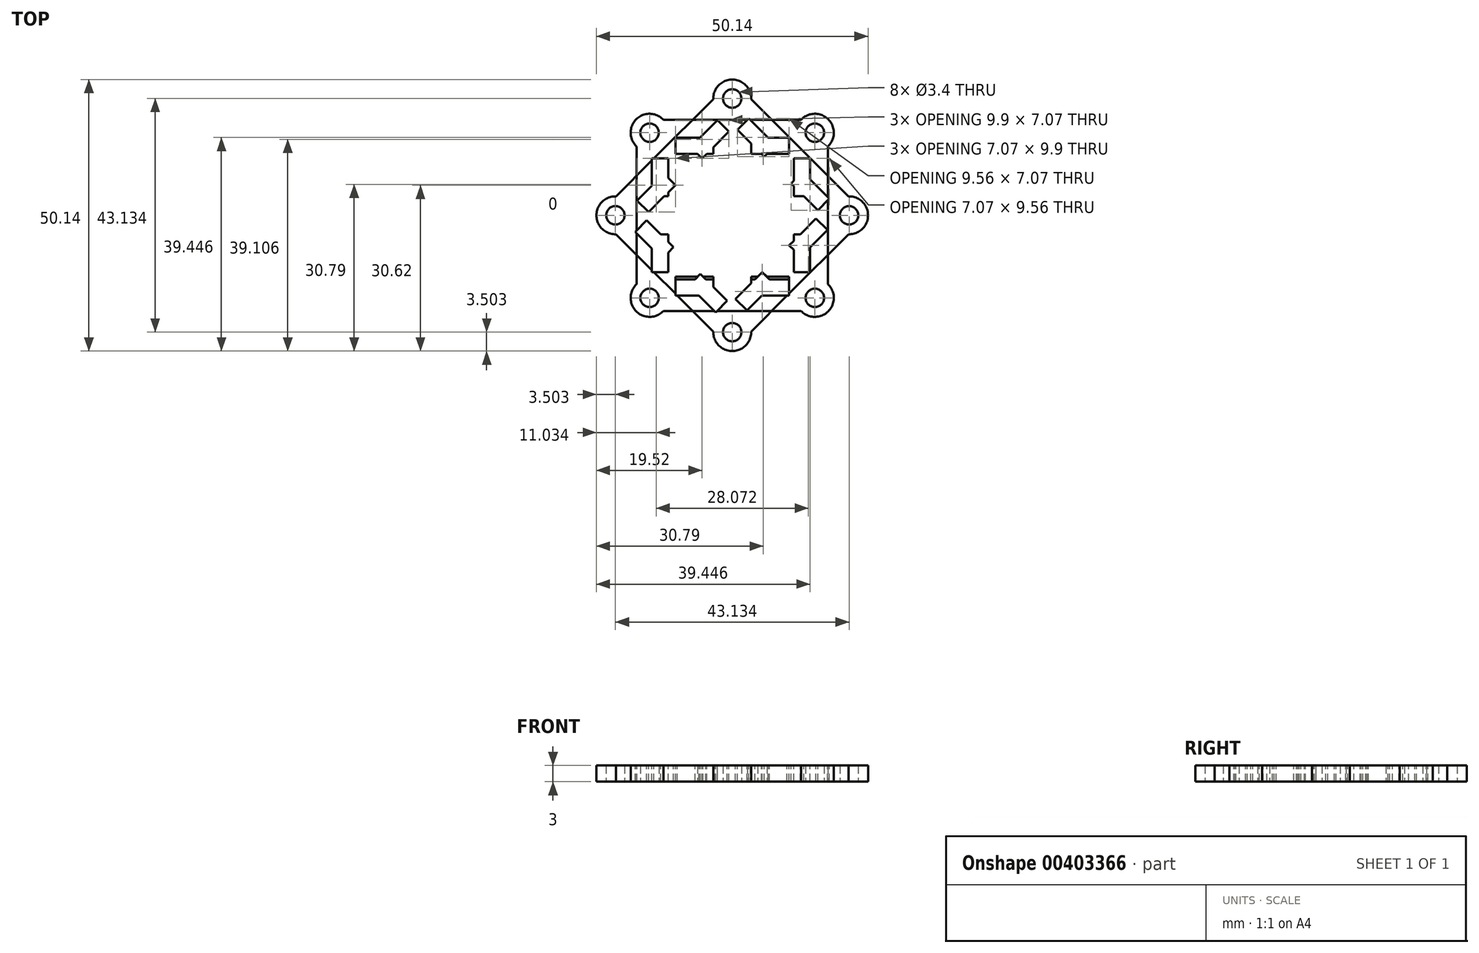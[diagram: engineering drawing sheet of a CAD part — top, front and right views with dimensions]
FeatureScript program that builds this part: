
annotation { "Feature Type Name" : "Feature", "Feature Type Description" : "" }
export const myFeature = defineFeature(function(context is Context, id is Id, definition is map)
    precondition{}
    {
        {
            assignVariable(context, id + "F0", {"name" : "padThickness", "anyValue" : 3});
        }
        {
            var Q0;
            Q0=qCreatedBy(makeId("Top.planeOp"),FACE);
            var sketch = newSketch(context, id + "F1", { "sketchPlane" : qUnion([Q0])});
            skLineSegment(sketch, "E0.bottom", {"start": v(15.25, -15.25) * mm, "end": v(-15.25, -15.25) * mm});
            skLineSegment(sketch, "E0.top", {"start": v(15.25, 15.25) * mm, "end": v(-15.25, 15.25) * mm});
            skLineSegment(sketch, "E0.left", {"start": v(15.25, -15.25) * mm, "end": v(15.25, 15.25) * mm});
            skLineSegment(sketch, "E0.right", {"start": v(-15.25, -15.25) * mm, "end": v(-15.25, 15.25) * mm});
            skPoint(sketch, "E0.middle", {"position": v(0, 0) * mm});
            skCircle(sketch, "E1", {"center": v(-15.25, 15.25) * mm, "radius": 1.7 * mm});
            skLineSegment(sketch, "E2", {"start": v(0, 15.25) * mm, "end": v(0, -15.25) * mm, "construction": true});
            skLineSegment(sketch, "E3", {"start": v(-15.25, 0) * mm, "end": v(15.25, 0) * mm, "construction": true});
            skCircle(sketch, "E4.MirrorC", {"center": v(15.25, 15.25) * mm, "radius": 1.7 * mm});
            skLineSegment(sketch, "E5.MirrorCS", {"start": v(15.25, 0) * mm, "end": v(-15.25, 0) * mm, "construction": true});
            skCircle(sketch, "E6.MirrorC", {"center": v(15.25, -15.25) * mm, "radius": 1.7 * mm});
            skCircle(sketch, "E7.MirrorC", {"center": v(-15.25, -15.25) * mm, "radius": 1.7 * mm});
            skCircle(sketch, "E8", {"center": v(-15.25, 15.25) * mm, "radius": 3.5 * mm});
            skCircle(sketch, "E9.MirrorC", {"center": v(15.25, 15.25) * mm, "radius": 3.5 * mm});
            skCircle(sketch, "E10.MirrorC", {"center": v(15.25, -15.25) * mm, "radius": 3.5 * mm});
            skCircle(sketch, "E11.MirrorC", {"center": v(-15.25, -15.25) * mm, "radius": 3.5 * mm});
            skLineSegment(sketch, "E12", {"start": v(-10.5, 15.25) * mm, "end": v(-10.5, -15.25) * mm, "construction": true});
            skLineSegment(sketch, "E13", {"start": v(10.5, 15.25) * mm, "end": v(10.5, -15.25) * mm, "construction": true});
            skLineSegment(sketch, "E14", {"start": v(-15.25, 17) * mm, "end": v(15.25, 17) * mm, "construction": true});
            skLineSegment(sketch, "E15", {"start": v(-15.25, -17) * mm, "end": v(15.25, -17) * mm, "construction": true});
            skLineSegment(sketch, "E16", {"start": v(-17.65, 12.7) * mm, "end": v(-17.65, -12.7) * mm});
            skLineSegment(sketch, "E17", {"start": v(-12.85, -12.7) * mm, "end": v(-12.85, 12.7) * mm});
            skLineSegment(sketch, "E18", {"start": v(-12.7, 17.65) * mm, "end": v(12.7, 17.65) * mm});
            skLineSegment(sketch, "E19", {"start": v(-12.7, 12.85) * mm, "end": v(12.7, 12.85) * mm});
            skLineSegment(sketch, "E20.MirrorCS", {"start": v(-12.7, -17.65) * mm, "end": v(12.7, -17.65) * mm});
            skLineSegment(sketch, "E21.MirrorCS", {"start": v(-12.7, -12.85) * mm, "end": v(12.7, -12.85) * mm});
            skLineSegment(sketch, "E22.MirrorCS", {"start": v(17.65, 12.7) * mm, "end": v(17.65, -12.7) * mm});
            skLineSegment(sketch, "E23.MirrorCS", {"start": v(12.85, -12.7) * mm, "end": v(12.85, 12.7) * mm});
            skPoint(sketch, "E24", {"position": v(0, 17) * mm});
            skPoint(sketch, "E25", {"position": v(0, 19.4) * mm});
            skSolve(sketch);
        }
        {
            var Q0;
            {var subQ1=sQuery(id+"F1.wireOp",EDGE,"E0.top");var subQ5=sQuery(id+"F1.wireOp",EDGE,"E8");var subQ7=makeQuery(id+"F1.imprint","INTERSECT",VERTEX,{"derivedFrom":[subQ1,subQ5]});Q0=makeQuery(id+"F1.imprint","IMPRINT",FACE,{"disambiguationData":[TD([[makeQuery(id+"F1.imprint","IMPRINT",EDGE,{"disambiguationData":[TD([[subQ7,-1.0]])],"derivedFrom":subQ1}),-1.0]])]});}
            var Q1;
            {var subQ0=sQuery(id+"F1.wireOp",EDGE,"E8");var subQ5=sQuery(id+"F1.wireOp",EDGE,"E0.top");var subQ9=makeQuery(id+"F1.imprint","INTERSECT",VERTEX,{"derivedFrom":[subQ5,subQ0]});Q1=makeQuery(id+"F1.imprint","IMPRINT",FACE,{"disambiguationData":[TD([[makeQuery(id+"F1.imprint","IMPRINT",EDGE,{"disambiguationData":[TD([[subQ9,-1.0]])],"derivedFrom":subQ5}),1.0]])]});}
            var Q2;
            {var subQ2=sQuery(id+"F1.wireOp",EDGE,"E0.top");var subQ4=sQuery(id+"F1.wireOp",EDGE,"E4.MirrorC");var subQ5=makeQuery(id+"F1.imprint","INTERSECT",VERTEX,{"derivedFrom":[subQ2,subQ4]});Q2=makeQuery(id+"F1.imprint","IMPRINT",FACE,{"disambiguationData":[TD([[makeQuery(id+"F1.imprint","IMPRINT",EDGE,{"disambiguationData":[TD([[subQ5,-1.0]])],"derivedFrom":subQ2}),-1.0]])]});}
            var Q3;
            {var subQ4=sQuery(id+"F1.wireOp",EDGE,"E4.MirrorC");var subQ5=sQuery(id+"F1.wireOp",EDGE,"E0.top");var subQ6=makeQuery(id+"F1.imprint","INTERSECT",VERTEX,{"derivedFrom":[subQ5,subQ4]});Q3=makeQuery(id+"F1.imprint","IMPRINT",FACE,{"disambiguationData":[TD([[makeQuery(id+"F1.imprint","IMPRINT",EDGE,{"disambiguationData":[TD([[subQ6,-1.0]])],"derivedFrom":subQ5}),1.0]])]});}
            var Q4;
            {var subQ5=sQuery(id+"F1.wireOp",EDGE,"E23.MirrorCS");Q4=makeQuery(id+"F1.imprint","IMPRINT",FACE,{"disambiguationData":[TD([[makeQuery(id+"F1.imprint","IMPRINT",EDGE,{"derivedFrom":subQ5}),-1.0]])]});}
            var Q5;
            {var subQ5=sQuery(id+"F1.wireOp",EDGE,"E19");Q5=makeQuery(id+"F1.imprint","IMPRINT",FACE,{"disambiguationData":[TD([[makeQuery(id+"F1.imprint","IMPRINT",EDGE,{"derivedFrom":subQ5}),1.0]])]});}
            var Q6;
            {var subQ5=sQuery(id+"F1.wireOp",EDGE,"E17");Q6=makeQuery(id+"F1.imprint","IMPRINT",FACE,{"disambiguationData":[TD([[makeQuery(id+"F1.imprint","IMPRINT",EDGE,{"derivedFrom":subQ5}),1.0]])]});}
            var Q7;
            {var subQ5=sQuery(id+"F1.wireOp",EDGE,"E16");Q7=makeQuery(id+"F1.imprint","IMPRINT",FACE,{"disambiguationData":[TD([[makeQuery(id+"F1.imprint","IMPRINT",EDGE,{"derivedFrom":subQ5}),1.0]])]});}
            var Q8;
            {var subQ5=sQuery(id+"F1.wireOp",EDGE,"E22.MirrorCS");Q8=makeQuery(id+"F1.imprint","IMPRINT",FACE,{"disambiguationData":[TD([[makeQuery(id+"F1.imprint","IMPRINT",EDGE,{"derivedFrom":subQ5}),-1.0]])]});}
            var Q9;
            {var subQ5=sQuery(id+"F1.wireOp",EDGE,"E21.MirrorCS");Q9=makeQuery(id+"F1.imprint","IMPRINT",FACE,{"disambiguationData":[TD([[makeQuery(id+"F1.imprint","IMPRINT",EDGE,{"derivedFrom":subQ5}),-1.0]])]});}
            var Q10;
            {var subQ5=sQuery(id+"F1.wireOp",EDGE,"E20.MirrorCS");Q10=makeQuery(id+"F1.imprint","IMPRINT",FACE,{"disambiguationData":[TD([[makeQuery(id+"F1.imprint","IMPRINT",EDGE,{"derivedFrom":subQ5}),1.0]])]});}
            var Q11;
            {var subQ5=sQuery(id+"F1.wireOp",EDGE,"E18");Q11=makeQuery(id+"F1.imprint","IMPRINT",FACE,{"disambiguationData":[TD([[makeQuery(id+"F1.imprint","IMPRINT",EDGE,{"derivedFrom":subQ5}),-1.0]])]});}
            var Q12;
            {var subQ0=sQuery(id+"F1.wireOp",EDGE,"E11.MirrorC");var subQ2=sQuery(id+"F1.wireOp",EDGE,"E0.bottom");var subQ3=makeQuery(id+"F1.imprint","INTERSECT",VERTEX,{"derivedFrom":[subQ2,subQ0]});Q12=makeQuery(id+"F1.imprint","IMPRINT",FACE,{"disambiguationData":[TD([[makeQuery(id+"F1.imprint","IMPRINT",EDGE,{"disambiguationData":[TD([[subQ3,-1.0]])],"derivedFrom":subQ2}),1.0]])]});}
            var Q13;
            {var subQ0=sQuery(id+"F1.wireOp",EDGE,"E11.MirrorC");var subQ5=sQuery(id+"F1.wireOp",EDGE,"E0.bottom");var subQ8=makeQuery(id+"F1.imprint","INTERSECT",VERTEX,{"derivedFrom":[subQ5,subQ0]});Q13=makeQuery(id+"F1.imprint","IMPRINT",FACE,{"disambiguationData":[TD([[makeQuery(id+"F1.imprint","IMPRINT",EDGE,{"disambiguationData":[TD([[subQ8,-1.0]])],"derivedFrom":subQ5}),-1.0]])]});}
            var Q14;
            {var subQ4=sQuery(id+"F1.wireOp",EDGE,"E6.MirrorC");var subQ5=sQuery(id+"F1.wireOp",EDGE,"E0.bottom");var subQ6=makeQuery(id+"F1.imprint","INTERSECT",VERTEX,{"derivedFrom":[subQ5,subQ4]});Q14=makeQuery(id+"F1.imprint","IMPRINT",FACE,{"disambiguationData":[TD([[makeQuery(id+"F1.imprint","IMPRINT",EDGE,{"disambiguationData":[TD([[subQ6,-1.0]])],"derivedFrom":subQ5}),-1.0]])]});}
            var Q15;
            {var subQ2=sQuery(id+"F1.wireOp",EDGE,"E0.bottom");var subQ4=sQuery(id+"F1.wireOp",EDGE,"E6.MirrorC");var subQ5=makeQuery(id+"F1.imprint","INTERSECT",VERTEX,{"derivedFrom":[subQ2,subQ4]});Q15=makeQuery(id+"F1.imprint","IMPRINT",FACE,{"disambiguationData":[TD([[makeQuery(id+"F1.imprint","IMPRINT",EDGE,{"disambiguationData":[TD([[subQ5,-1.0]])],"derivedFrom":subQ2}),1.0]])]});}
            var Q16;
            {var subQ0=sQuery(id+"F1.wireOp",EDGE,"E17");Q16=makeQuery(id+"F1.imprint","IMPRINT",FACE,{"disambiguationData":[TD([[makeQuery(id+"F1.imprint","IMPRINT",EDGE,{"derivedFrom":subQ0}),-1.0]])]});}
            extrude(context, id + "F2", {"entities" : qUnion([Q0, Q1, Q2, Q3, Q4, Q5, Q6, Q7, Q8, Q9, Q10, Q11, Q12, Q13, Q14, Q15, Q16]), "depth" : (getVariable(context, 'padThickness')) * mm});
        }
        {
            var Q0;
            Q0=qCreatedBy(makeId("Front.planeOp"),FACE);
            var sketch = newSketch(context, id + "F3", { "sketchPlane" : qUnion([Q0])});
            skLineSegment(sketch, "E26", {"start": v(0, 0) * mm, "end": v(0, 87.17) * mm, "construction": true});
            skSolve(sketch);
        }
        {
            var Q0;
            Q0=makeQuery(id+"F2.opExtrude","SWEPT_BODY",BODY,{"disambiguationData":[OSD([sQuery(id+"F1.wireOp",EDGE,"E1"),sQuery(id+"F1.wireOp",EDGE,"E4.MirrorC"),sQuery(id+"F1.wireOp",EDGE,"E6.MirrorC"),sQuery(id+"F1.wireOp",EDGE,"E7.MirrorC"),sQuery(id+"F1.wireOp",EDGE,"E8"),sQuery(id+"F1.wireOp",EDGE,"E9.MirrorC"),sQuery(id+"F1.wireOp",EDGE,"E10.MirrorC"),sQuery(id+"F1.wireOp",EDGE,"E11.MirrorC"),sQuery(id+"F1.wireOp",EDGE,"E16"),sQuery(id+"F1.wireOp",EDGE,"E18"),sQuery(id+"F1.wireOp",EDGE,"E20.MirrorCS"),sQuery(id+"F1.wireOp",EDGE,"E22.MirrorCS")])]});
            var Q1;
            Q1=sQuery(id+"F3.wireOp",EDGE,"E26");
            transform(context, id + "F4", {"entities" : qUnion([Q0]), "transformType" : TransformType.ROTATION, "transformAxis" : qUnion([Q1]), "angle" : 45 * degree, "makeCopy" : true});
        }
        {
            var Q0;
            Q0=makeQuery(id+"F2.opExtrude","SWEPT_BODY",BODY,{"disambiguationData":[OSD([sQuery(id+"F1.wireOp",EDGE,"E1"),sQuery(id+"F1.wireOp",EDGE,"E4.MirrorC"),sQuery(id+"F1.wireOp",EDGE,"E6.MirrorC"),sQuery(id+"F1.wireOp",EDGE,"E7.MirrorC"),sQuery(id+"F1.wireOp",EDGE,"E8"),sQuery(id+"F1.wireOp",EDGE,"E9.MirrorC"),sQuery(id+"F1.wireOp",EDGE,"E10.MirrorC"),sQuery(id+"F1.wireOp",EDGE,"E11.MirrorC"),sQuery(id+"F1.wireOp",EDGE,"E16"),sQuery(id+"F1.wireOp",EDGE,"E18"),sQuery(id+"F1.wireOp",EDGE,"E20.MirrorCS"),sQuery(id+"F1.wireOp",EDGE,"E22.MirrorCS")])]});
            var Q1;
            Q1=makeQuery(id+"F4.opPattern","COPY",BODY,{"derivedFrom":makeQuery(id+"F2.opExtrude","SWEPT_BODY",BODY,{"disambiguationData":[OSD([sQuery(id+"F1.wireOp",EDGE,"E1"),sQuery(id+"F1.wireOp",EDGE,"E4.MirrorC"),sQuery(id+"F1.wireOp",EDGE,"E6.MirrorC"),sQuery(id+"F1.wireOp",EDGE,"E7.MirrorC"),sQuery(id+"F1.wireOp",EDGE,"E8"),sQuery(id+"F1.wireOp",EDGE,"E9.MirrorC"),sQuery(id+"F1.wireOp",EDGE,"E10.MirrorC"),sQuery(id+"F1.wireOp",EDGE,"E11.MirrorC"),sQuery(id+"F1.wireOp",EDGE,"E16"),sQuery(id+"F1.wireOp",EDGE,"E18"),sQuery(id+"F1.wireOp",EDGE,"E20.MirrorCS"),sQuery(id+"F1.wireOp",EDGE,"E22.MirrorCS")])]}),"instanceName":"1"});
            booleanBodies(context, id + "F5", {"operationType" : BooleanOperationType.UNION, "tools" : qUnion([Q0, Q1])});
        }
        {
            var Q0;
            Q0=makeQuery(id+"F2.opExtrude","CAP_FACE",FACE,{"disambiguationData":[OSD([sQuery(id+"F1.wireOp",EDGE,"E1"),sQuery(id+"F1.wireOp",EDGE,"E4.MirrorC"),sQuery(id+"F1.wireOp",EDGE,"E6.MirrorC"),sQuery(id+"F1.wireOp",EDGE,"E7.MirrorC"),sQuery(id+"F1.wireOp",EDGE,"E8"),sQuery(id+"F1.wireOp",EDGE,"E9.MirrorC"),sQuery(id+"F1.wireOp",EDGE,"E10.MirrorC"),sQuery(id+"F1.wireOp",EDGE,"E11.MirrorC"),sQuery(id+"F1.wireOp",EDGE,"E16"),sQuery(id+"F1.wireOp",EDGE,"E18"),sQuery(id+"F1.wireOp",EDGE,"E20.MirrorCS"),sQuery(id+"F1.wireOp",EDGE,"E22.MirrorCS")])],"isStart":false});
            var sketch = newSketch(context, id + "F6", { "sketchPlane" : qUnion([Q0])});
            skLineSegment(sketch, "E27.0", {"start": v(-10.5, 15.25) * mm, "end": v(-10.5, -15.25) * mm, "construction": true});
            skLineSegment(sketch, "E27.1", {"start": v(-12.7, 12.85) * mm, "end": v(12.7, 12.85) * mm, "construction": true});
            skLineSegment(sketch, "E27.2", {"start": v(10.5, 15.25) * mm, "end": v(10.5, -15.25) * mm, "construction": true});
            skLineSegment(sketch, "E27.3", {"start": v(-12.7, -12.85) * mm, "end": v(12.7, -12.85) * mm, "construction": true});
            skText(sketch, "E28", { "text": "tits", "fontName": "AllertaStencil-Regular.ttf"});
            skPoint(sketch, "E29", {"position": v(0, 0) * mm});
            const initialGuessF6  = {"E28": [-0.015, -0.00666, 1, 0, 0.01332]};
            skSetInitialGuess(sketch, initialGuessF6);
            skSolve(sketch);
        }
        {
            var Q0;
            {var subQ0=makeQuery(id+"F2.opExtrude","CAP_FACE",FACE,{"disambiguationData":[OSD([sQuery(id+"F1.wireOp",EDGE,"E1"),sQuery(id+"F1.wireOp",EDGE,"E4.MirrorC"),sQuery(id+"F1.wireOp",EDGE,"E6.MirrorC"),sQuery(id+"F1.wireOp",EDGE,"E7.MirrorC"),sQuery(id+"F1.wireOp",EDGE,"E8"),sQuery(id+"F1.wireOp",EDGE,"E9.MirrorC"),sQuery(id+"F1.wireOp",EDGE,"E10.MirrorC"),sQuery(id+"F1.wireOp",EDGE,"E11.MirrorC"),sQuery(id+"F1.wireOp",EDGE,"E16"),sQuery(id+"F1.wireOp",EDGE,"E18"),sQuery(id+"F1.wireOp",EDGE,"E20.MirrorCS"),sQuery(id+"F1.wireOp",EDGE,"E22.MirrorCS")])],"isStart":false});Q0=makeQuery(id+"F5.opBoolean","MERGE",FACE,{"derivedFrom":[subQ0,makeQuery(id+"F4.opPattern","COPY",FACE,{"derivedFrom":subQ0,"instanceName":"1"})]});}
            var sketch = newSketch(context, id + "F7", { "sketchPlane" : qUnion([Q0])});
            skLineSegment(sketch, "E30.0", {"start": v(15.25, -15.25) * mm, "end": v(15.25, 15.25) * mm, "construction": true});
            skLineSegment(sketch, "E30.1", {"start": v(15.25, 15.25) * mm, "end": v(-15.25, 15.25) * mm, "construction": true});
            skLineSegment(sketch, "E30.2", {"start": v(-15.25, -15.25) * mm, "end": v(-15.25, 15.25) * mm, "construction": true});
            skLineSegment(sketch, "E30.3", {"start": v(15.25, -15.25) * mm, "end": v(-15.25, -15.25) * mm, "construction": true});
            skLineSegment(sketch, "E31", {"start": v(-15.25, 15.25) * mm, "end": v(15.25, -15.25) * mm, "construction": true});
            skLineSegment(sketch, "E32", {"start": v(21.57, 0) * mm, "end": v(-21.57, 0) * mm, "construction": true});
            skLineSegment(sketch, "E33", {"start": v(0, 21.57) * mm, "end": v(0, -21.57) * mm, "construction": true});
            skLineSegment(sketch, "E34", {"start": v(-15.25, -15.25) * mm, "end": v(15.25, 15.25) * mm, "construction": true});
            skCircle(sketch, "E35.0", {"center": v(-15.25, 15.25) * mm, "radius": 3.5 * mm, "construction": true});
            skLineSegment(sketch, "E36.0", {"start": v(-12.85, -12.7) * mm, "end": v(-12.85, -5.97) * mm, "construction": true});
            skLineSegment(sketch, "E37.0", {"start": v(-9.46, 12.85) * mm, "end": v(9.46, 12.85) * mm});
            skLineSegment(sketch, "E37.1", {"start": v(12.85, -12.7) * mm, "end": v(12.85, -5.97) * mm, "construction": true});
            skLineSegment(sketch, "E38.0", {"start": v(-9.46, -12.85) * mm, "end": v(9.46, -12.85) * mm});
            skCircle(sketch, "E39.0", {"center": v(15.25, -15.25) * mm, "radius": 3.5 * mm, "construction": true});
            skCircle(sketch, "E40.0", {"center": v(-15.25, -15.25) * mm, "radius": 3.5 * mm, "construction": true});
            skLineSegment(sketch, "E41.0", {"start": v(-12.7, 17.65) * mm, "end": v(12.7, 17.65) * mm});
            skLineSegment(sketch, "E42.0", {"start": v(-15.25, -17) * mm, "end": v(15.25, -17) * mm, "construction": true});
            skLineSegment(sketch, "E43.0", {"start": v(-17.65, 12.7) * mm, "end": v(-17.65, -12.7) * mm, "construction": true});
            skLineSegment(sketch, "E44.0", {"start": v(17.65, 12.7) * mm, "end": v(17.65, -12.7) * mm, "construction": true});
            skPoint(sketch, "E45", {"position": v(-12.7, 12.85) * mm});
            skPoint(sketch, "E46", {"position": v(-12.85, 12.7) * mm});
            skCircle(sketch, "E47.0", {"center": v(15.25, 15.25) * mm, "radius": 3.5 * mm, "construction": true});
            skLineSegment(sketch, "E48", {"start": v(-17.65, 7.31) * mm, "end": v(-2.4, 7.31) * mm, "construction": true});
            skLineSegment(sketch, "E49", {"start": v(-17.65, -7.31) * mm, "end": v(-2.4, -7.31) * mm, "construction": true});
            skPoint(sketch, "E50", {"position": v(0, 7.31) * mm});
            skPoint(sketch, "E51", {"position": v(0, -7.31) * mm});
            skArc(sketch, "E52", {"start": v(12.85, 5.97) * mm, "mid": v(11.38, 6.26) * mm, "end": v(9.91, 6.52) * mm});
            skPoint(sketch, "E53", {"position": v(-12.85, 5.97) * mm});
            skPoint(sketch, "E54", {"position": v(12.85, 5.97) * mm});
            skPoint(sketch, "E55.MirrorP", {"position": v(12.85, -5.97) * mm});
            skPoint(sketch, "E56.MirrorP", {"position": v(-12.85, -5.97) * mm});
            skArc(sketch, "E57.MirrorCS", {"start": v(12.85, -5.97) * mm, "mid": v(11.38, -6.26) * mm, "end": v(9.91, -6.52) * mm});
            skPoint(sketch, "E58.trimOffspring.end.orphan", {"position": v(-21.46, 3.5) * mm});
            skPoint(sketch, "E59.orphan", {"position": v(21.46, 3.5) * mm});
            skPoint(sketch, "E60.orphan", {"position": v(21.46, -3.5) * mm});
            skPoint(sketch, "E61.orphan", {"position": v(-21.46, -3.5) * mm});
            skLineSegment(sketch, "E62.0", {"start": v(-2.4, 12.85) * mm, "end": v(-2.4, 7.26) * mm});
            skPoint(sketch, "E63.orphan", {"position": v(-2.4, 21.57) * mm});
            skPoint(sketch, "E64.orphan", {"position": v(2.4, 21.57) * mm});
            skPoint(sketch, "E65.orphan", {"position": v(2.4, -21.57) * mm});
            skPoint(sketch, "E66.orphan", {"position": v(-2.4, -21.57) * mm});
            skLineSegment(sketch, "E67.0", {"start": v(-9.46, 12.85) * mm, "end": v(16.95, -13.55) * mm, "construction": true});
            skLineSegment(sketch, "E68.MirrorCS", {"start": v(-12.85, 9.46) * mm, "end": v(13.55, -16.95) * mm, "construction": true});
            skPoint(sketch, "E69.orphan", {"position": v(-13.55, 16.95) * mm});
            skPoint(sketch, "E70.orphan", {"position": v(-16.95, 13.55) * mm});
            skLineSegment(sketch, "E71.0", {"start": v(-16.95, -13.55) * mm, "end": v(-15.25, -11.86) * mm, "construction": true});
            skLineSegment(sketch, "E72.MirrorCS", {"start": v(-13.55, -16.95) * mm, "end": v(16.95, 13.55) * mm, "construction": true});
            skPoint(sketch, "E73.orphan", {"position": v(12.7, 12.85) * mm});
            skPoint(sketch, "E74.orphan", {"position": v(12.85, 12.7) * mm});
            skPoint(sketch, "E75.orphan", {"position": v(-12.7, -12.85) * mm});
            skPoint(sketch, "E76.orphan", {"position": v(12.7, -12.85) * mm});
            skLineSegment(sketch, "E77.trimOffspring", {"start": v(-12.85, 5.97) * mm, "end": v(-12.85, 9.46) * mm, "construction": true});
            skLineSegment(sketch, "E78.trimOffspring", {"start": v(12.85, 5.97) * mm, "end": v(12.85, 9.46) * mm, "construction": true});
            skLineSegment(sketch, "E79", {"start": v(-12.85, 9.46) * mm, "end": v(-12.85, 5.97) * mm});
            skLineSegment(sketch, "E80", {"start": v(-12.85, -5.97) * mm, "end": v(-12.85, -9.46) * mm});
            skLineSegment(sketch, "E81.trimOffspring", {"start": v(-15.15, -11.75) * mm, "end": v(13.55, 16.95) * mm, "construction": true});
            skLineSegment(sketch, "E82", {"start": v(-9.46, 12.85) * mm, "end": v(-3.8, 7.2) * mm});
            skLineSegment(sketch, "E83", {"start": v(-9.91, 6.52) * mm, "end": v(-12.85, 9.46) * mm});
            skLineSegment(sketch, "E84", {"start": v(9.46, 12.85) * mm, "end": v(3.8, 7.2) * mm});
            skLineSegment(sketch, "E85", {"start": v(12.85, 9.46) * mm, "end": v(9.91, 6.52) * mm});
            skLineSegment(sketch, "E86", {"start": v(-9.91, -6.52) * mm, "end": v(-12.85, -9.46) * mm});
            skLineSegment(sketch, "E87", {"start": v(-9.46, -12.85) * mm, "end": v(-3.8, -7.2) * mm});
            skLineSegment(sketch, "E88", {"start": v(3.8, -7.2) * mm, "end": v(9.46, -12.85) * mm});
            skLineSegment(sketch, "E89", {"start": v(9.91, -6.52) * mm, "end": v(12.85, -9.46) * mm});
            skLineSegment(sketch, "E90", {"start": v(12.85, -9.46) * mm, "end": v(12.85, -5.97) * mm});
            skLineSegment(sketch, "E91", {"start": v(12.85, 9.46) * mm, "end": v(12.85, 5.97) * mm});
            skLineSegment(sketch, "E92.MirrorCS", {"start": v(2.4, 12.85) * mm, "end": v(2.4, 7.26) * mm});
            skLineSegment(sketch, "E93.MirrorCS", {"start": v(-2.4, -12.85) * mm, "end": v(-2.4, -7.26) * mm});
            skLineSegment(sketch, "E94.MirrorCS", {"start": v(2.4, -12.85) * mm, "end": v(2.4, -7.26) * mm});
            skArc(sketch, "E95.trimOffspring", {"start": v(-9.91, 6.52) * mm, "mid": v(-11.38, 6.26) * mm, "end": v(-12.85, 5.97) * mm});
            skArc(sketch, "E96.trimOffspring", {"start": v(-2.4, 7.26) * mm, "mid": v(-3.1, 7.23) * mm, "end": v(-3.8, 7.2) * mm});
            skLineSegment(sketch, "E97.trimOffspring", {"start": v(0, 7.31) * mm, "end": v(17.65, 7.31) * mm, "construction": true});
            skArc(sketch, "E98.trimOffspring", {"start": v(3.8, 7.2) * mm, "mid": v(3.1, 7.23) * mm, "end": v(2.4, 7.26) * mm});
            skArc(sketch, "E99.trimOffspring", {"start": v(-9.91, -6.52) * mm, "mid": v(-11.38, -6.26) * mm, "end": v(-12.85, -5.97) * mm});
            skLineSegment(sketch, "E100.trimOffspring", {"start": v(2.4, -7.31) * mm, "end": v(17.65, -7.31) * mm, "construction": true});
            skArc(sketch, "E101.trimOffspring", {"start": v(3.8, -7.2) * mm, "mid": v(3.1, -7.23) * mm, "end": v(2.4, -7.26) * mm});
            skArc(sketch, "E102.trimOffspring", {"start": v(-2.4, -7.26) * mm, "mid": v(-3.1, -7.23) * mm, "end": v(-3.8, -7.2) * mm});
            skSolve(sketch);
        }
        {
            var Q0;
            {var subQ0=makeQuery(id+"F2.opExtrude","CAP_FACE",FACE,{"disambiguationData":[OSD([sQuery(id+"F1.wireOp",EDGE,"E1"),sQuery(id+"F1.wireOp",EDGE,"E4.MirrorC"),sQuery(id+"F1.wireOp",EDGE,"E6.MirrorC"),sQuery(id+"F1.wireOp",EDGE,"E7.MirrorC"),sQuery(id+"F1.wireOp",EDGE,"E8"),sQuery(id+"F1.wireOp",EDGE,"E9.MirrorC"),sQuery(id+"F1.wireOp",EDGE,"E10.MirrorC"),sQuery(id+"F1.wireOp",EDGE,"E11.MirrorC"),sQuery(id+"F1.wireOp",EDGE,"E16"),sQuery(id+"F1.wireOp",EDGE,"E18"),sQuery(id+"F1.wireOp",EDGE,"E20.MirrorCS"),sQuery(id+"F1.wireOp",EDGE,"E22.MirrorCS")])],"isStart":false});Q0=makeQuery(id+"F5.opBoolean","MERGE",FACE,{"derivedFrom":[subQ0,makeQuery(id+"F4.opPattern","COPY",FACE,{"derivedFrom":subQ0,"instanceName":"1"})]});}
            var sketch = newSketch(context, id + "F8", { "sketchPlane" : qUnion([Q0])});
            skLineSegment(sketch, "E103", {"start": v(-17.65, 7.31) * mm, "end": v(-17.65, -7.31) * mm});
            skLineSegment(sketch, "E104", {"start": v(-7.31, -17.65) * mm, "end": v(7.31, -17.65) * mm});
            skLineSegment(sketch, "E105", {"start": v(17.65, -7.31) * mm, "end": v(17.65, 7.31) * mm});
            skLineSegment(sketch, "E106", {"start": v(7.31, 17.65) * mm, "end": v(-7.31, 17.65) * mm});
            skSolve(sketch);
        }
        {
            var Q0;
            Q0=makeQuery(id+"F8.imprint","IMPRINT",FACE,{"disambiguationData":[TD([[makeQuery(id+"F8.imprint","IMPRINT",EDGE,{"derivedFrom":sQuery(id+"F8.wireOp",EDGE,"E106")}),-1.0]])]});
            var Q1;
            Q1=makeQuery(id+"F8.imprint","IMPRINT",FACE,{"disambiguationData":[TD([[makeQuery(id+"F8.imprint","IMPRINT",EDGE,{"derivedFrom":sQuery(id+"F8.wireOp",EDGE,"E105")}),-1.0]])]});
            var Q2;
            Q2=makeQuery(id+"F8.imprint","IMPRINT",FACE,{"disambiguationData":[TD([[makeQuery(id+"F8.imprint","IMPRINT",EDGE,{"derivedFrom":sQuery(id+"F8.wireOp",EDGE,"E104")}),-1.0]])]});
            var Q3;
            Q3=makeQuery(id+"F8.imprint","IMPRINT",FACE,{"disambiguationData":[TD([[makeQuery(id+"F8.imprint","IMPRINT",EDGE,{"derivedFrom":sQuery(id+"F8.wireOp",EDGE,"E103")}),-1.0]])]});
            extrude(context, id + "F9", {"entities" : qUnion([Q0, Q1, Q2, Q3]), "operationType" : NewBodyOperationType.REMOVE, "endBound" : BoundingType.THROUGH_ALL, "oppositeDirection" : true, "depth" : 25 * mm});
        }
        {
            var Q0;
            Q0=makeQuery(id+"F7.imprint","IMPRINT",FACE,{"disambiguationData":[TD([[makeQuery(id+"F7.imprint","IMPRINT",EDGE,{"derivedFrom":sQuery(id+"F7.wireOp",EDGE,"E52")}),1.0]])]});
            var sketch = newSketch(context, id + "F10", { "sketchPlane" : qUnion([Q0])});
            skLineSegment(sketch, "E107.0", {"start": v(0, 21.57) * mm, "end": v(0, -21.57) * mm, "construction": true});
            skLineSegment(sketch, "E108.0", {"start": v(21.57, 0) * mm, "end": v(-21.57, 0) * mm, "construction": true});
            skLineSegment(sketch, "E109.0", {"start": v(-12.7, 17.65) * mm, "end": v(12.7, 17.65) * mm});
            skLineSegment(sketch, "E110.0", {"start": v(-17.65, 12.7) * mm, "end": v(-17.65, -12.7) * mm, "construction": true});
            skLineSegment(sketch, "E111.0", {"start": v(17.65, 12.7) * mm, "end": v(17.65, -12.7) * mm, "construction": true});
            skLineSegment(sketch, "E112.0", {"start": v(-9.46, 12.85) * mm, "end": v(9.46, 12.85) * mm, "construction": true});
            skPoint(sketch, "E113", {"position": v(0, 12.85) * mm});
            skPoint(sketch, "E114", {"position": v(57.37, 5.4) * mm});
            skLineSegment(sketch, "E115", {"start": v(-7, 17.65) * mm, "end": v(-7, -17.67) * mm, "construction": true});
            skLineSegment(sketch, "E116", {"start": v(7, 17.65) * mm, "end": v(7, -17.67) * mm, "construction": true});
            skPoint(sketch, "E117", {"position": v(-7, 12.85) * mm});
            skPoint(sketch, "E118", {"position": v(7, 12.85) * mm});
            skLineSegment(sketch, "E119.bottom", {"start": v(-3.5, 11.35) * mm, "end": v(-10.5, 11.35) * mm});
            skLineSegment(sketch, "E119.top", {"start": v(-3.5, 14.35) * mm, "end": v(-10.5, 14.35) * mm});
            skLineSegment(sketch, "E119.left", {"start": v(-3.5, 11.35) * mm, "end": v(-3.5, 14.35) * mm});
            skLineSegment(sketch, "E119.right", {"start": v(-10.5, 11.35) * mm, "end": v(-10.5, 14.35) * mm});
            skLineSegment(sketch, "E120.MirrorCS", {"start": v(10.5, 11.35) * mm, "end": v(10.5, 14.35) * mm});
            skLineSegment(sketch, "E121.MirrorCS", {"start": v(3.5, 11.35) * mm, "end": v(3.5, 14.35) * mm});
            skLineSegment(sketch, "E122.MirrorCS", {"start": v(3.5, 14.35) * mm, "end": v(10.5, 14.35) * mm});
            skLineSegment(sketch, "E123.MirrorCS", {"start": v(3.5, 11.35) * mm, "end": v(10.5, 11.35) * mm});
            skLineSegment(sketch, "E124.MirrorCS", {"start": v(10.5, 14.35) * mm, "end": v(10.5, 11.35) * mm});
            skLineSegment(sketch, "E125.MirrorCS", {"start": v(-10.5, 14.35) * mm, "end": v(-10.5, 11.35) * mm});
            skLineSegment(sketch, "E126.MirrorCS", {"start": v(-3.5, 14.35) * mm, "end": v(-3.5, 11.35) * mm});
            skLineSegment(sketch, "E127.MirrorCS", {"start": v(3.5, 14.35) * mm, "end": v(3.5, 11.35) * mm});
            skLineSegment(sketch, "E128.MirrorCS", {"start": v(21.57, 25.7) * mm, "end": v(-21.57, 25.7) * mm, "construction": true});
            skLineSegment(sketch, "E129.MirrorCS", {"start": v(10.5, -11.35) * mm, "end": v(10.5, -14.35) * mm});
            skLineSegment(sketch, "E130.MirrorCS", {"start": v(3.5, -14.35) * mm, "end": v(10.5, -14.35) * mm});
            skLineSegment(sketch, "E131.MirrorCS", {"start": v(3.5, -11.35) * mm, "end": v(10.5, -11.35) * mm});
            skLineSegment(sketch, "E132.MirrorCS", {"start": v(3.5, -11.35) * mm, "end": v(3.5, -14.35) * mm});
            skLineSegment(sketch, "E133.MirrorCS", {"start": v(-3.5, -11.35) * mm, "end": v(-3.5, -14.35) * mm});
            skLineSegment(sketch, "E134.MirrorCS", {"start": v(-3.5, -11.35) * mm, "end": v(-10.5, -11.35) * mm});
            skLineSegment(sketch, "E135.MirrorCS", {"start": v(-3.5, -14.35) * mm, "end": v(-10.5, -14.35) * mm});
            skLineSegment(sketch, "E136.MirrorCS", {"start": v(-10.5, -11.35) * mm, "end": v(-10.5, -14.35) * mm});
            skLineSegment(sketch, "E137.MirrorCS", {"start": v(-9.46, -12.85) * mm, "end": v(9.46, -12.85) * mm, "construction": true});
            skSolve(sketch);
        }
        {
            var Q0;
            {var subQ5=sQuery(id+"F10.wireOp",EDGE,"E119.top");Q0=makeQuery(id+"F10.imprint","IMPRINT",FACE,{"disambiguationData":[TD([[makeQuery(id+"F10.imprint","IMPRINT",EDGE,{"derivedFrom":subQ5}),1.0]])]});}
            var Q1;
            {var subQ0=sQuery(id+"F10.wireOp",EDGE,"E119.bottom");var subQ1=sQuery(id+"F10.wireOp",EDGE,"E119.left");var subQ2=makeQuery(id+"F10.imprint","INTERSECT",VERTEX,{"derivedFrom":[subQ1,subQ0]});Q1=makeQuery(id+"F10.imprint","IMPRINT",FACE,{"disambiguationData":[TD([[makeQuery(id+"F10.imprint","IMPRINT",EDGE,{"disambiguationData":[TD([[subQ2,-1.0]])],"derivedFrom":subQ0}),-1.0]])]});}
            var Q2;
            {var subQ0=sQuery(id+"F10.wireOp",EDGE,"E127.MirrorCS");var subQ1=sQuery(id+"F10.wireOp",EDGE,"E123.MirrorCS");var subQ2=makeQuery(id+"F10.imprint","INTERSECT",VERTEX,{"derivedFrom":[subQ1,subQ0]});Q2=makeQuery(id+"F10.imprint","IMPRINT",FACE,{"disambiguationData":[TD([[makeQuery(id+"F10.imprint","IMPRINT",EDGE,{"disambiguationData":[TD([[subQ2,-1.0]])],"derivedFrom":subQ1}),1.0]])]});}
            var Q3;
            {var subQ1=sQuery(id+"F10.wireOp",EDGE,"E122.MirrorCS");Q3=makeQuery(id+"F10.imprint","IMPRINT",FACE,{"disambiguationData":[TD([[makeQuery(id+"F10.imprint","IMPRINT",EDGE,{"derivedFrom":subQ1}),-1.0]])]});}
            var Q4;
            {var subQ0=sQuery(id+"F10.wireOp",EDGE,"E132.MirrorCS");var subQ1=sQuery(id+"F10.wireOp",EDGE,"E131.MirrorCS");var subQ2=makeQuery(id+"F10.imprint","INTERSECT",VERTEX,{"derivedFrom":[subQ1,subQ0]});Q4=makeQuery(id+"F10.imprint","IMPRINT",FACE,{"disambiguationData":[TD([[makeQuery(id+"F10.imprint","IMPRINT",EDGE,{"disambiguationData":[TD([[subQ2,-1.0]])],"derivedFrom":subQ1}),-1.0]])]});}
            var Q5;
            {var subQ1=sQuery(id+"F10.wireOp",EDGE,"E135.MirrorCS");Q5=makeQuery(id+"F10.imprint","IMPRINT",FACE,{"disambiguationData":[TD([[makeQuery(id+"F10.imprint","IMPRINT",EDGE,{"derivedFrom":subQ1}),-1.0]])]});}
            var Q6;
            {var subQ0=sQuery(id+"F10.wireOp",EDGE,"E134.MirrorCS");var subQ1=sQuery(id+"F10.wireOp",EDGE,"E133.MirrorCS");var subQ2=makeQuery(id+"F10.imprint","INTERSECT",VERTEX,{"derivedFrom":[subQ1,subQ0]});Q6=makeQuery(id+"F10.imprint","IMPRINT",FACE,{"disambiguationData":[TD([[makeQuery(id+"F10.imprint","IMPRINT",EDGE,{"disambiguationData":[TD([[subQ2,-1.0]])],"derivedFrom":subQ0}),1.0]])]});}
            var Q7;
            {var subQ0=sQuery(id+"F10.wireOp",EDGE,"E119.bottom");var subQ1=sQuery(id+"F10.wireOp",EDGE,"E119.right");var subQ2=makeQuery(id+"F10.imprint","INTERSECT",VERTEX,{"derivedFrom":[subQ1,subQ0]});Q7=makeQuery(id+"F10.imprint","IMPRINT",FACE,{"disambiguationData":[TD([[makeQuery(id+"F10.imprint","IMPRINT",EDGE,{"disambiguationData":[TD([[subQ2,-1.0]])],"derivedFrom":subQ1}),-1.0]])]});}
            var Q8;
            {var subQ0=sQuery(id+"F10.wireOp",EDGE,"E123.MirrorCS");var subQ1=sQuery(id+"F10.wireOp",EDGE,"E124.MirrorCS");var subQ2=makeQuery(id+"F10.imprint","INTERSECT",VERTEX,{"derivedFrom":[subQ1,subQ0]});Q8=makeQuery(id+"F10.imprint","IMPRINT",FACE,{"disambiguationData":[TD([[makeQuery(id+"F10.imprint","IMPRINT",EDGE,{"disambiguationData":[TD([[subQ2,1.0]])],"derivedFrom":subQ1}),-1.0]])]});}
            var Q9;
            {var subQ0=sQuery(id+"F10.wireOp",EDGE,"E136.MirrorCS");var subQ1=sQuery(id+"F10.wireOp",EDGE,"E134.MirrorCS");var subQ2=makeQuery(id+"F10.imprint","INTERSECT",VERTEX,{"derivedFrom":[subQ1,subQ0]});Q9=makeQuery(id+"F10.imprint","IMPRINT",FACE,{"disambiguationData":[TD([[makeQuery(id+"F10.imprint","IMPRINT",EDGE,{"disambiguationData":[TD([[subQ2,1.0]])],"derivedFrom":subQ1}),1.0]])]});}
            var Q10;
            {var subQ0=sQuery(id+"F10.wireOp",EDGE,"E130.MirrorCS");Q10=makeQuery(id+"F10.imprint","IMPRINT",FACE,{"disambiguationData":[TD([[makeQuery(id+"F10.imprint","IMPRINT",EDGE,{"derivedFrom":subQ0}),1.0]])]});}
            var Q11;
            {var subQ0=sQuery(id+"F10.wireOp",EDGE,"E131.MirrorCS");var subQ1=sQuery(id+"F10.wireOp",EDGE,"E129.MirrorCS");var subQ2=makeQuery(id+"F10.imprint","INTERSECT",VERTEX,{"derivedFrom":[subQ1,subQ0]});Q11=makeQuery(id+"F10.imprint","IMPRINT",FACE,{"disambiguationData":[TD([[makeQuery(id+"F10.imprint","IMPRINT",EDGE,{"disambiguationData":[TD([[subQ2,-1.0]])],"derivedFrom":subQ1}),-1.0]])]});}
            extrude(context, id + "F11", {"entities" : qUnion([Q0, Q1, Q2, Q3, Q4, Q5, Q6, Q7, Q8, Q9, Q10, Q11]), "operationType" : NewBodyOperationType.REMOVE, "endBound" : BoundingType.THROUGH_ALL, "oppositeDirection" : true, "depth" : 25 * mm});
        }
        {
            var Q0;
            Q0=makeQuery(id+"F2.opExtrude","SWEPT_BODY",BODY,{"disambiguationData":[OSD([sQuery(id+"F1.wireOp",EDGE,"E1"),sQuery(id+"F1.wireOp",EDGE,"E4.MirrorC"),sQuery(id+"F1.wireOp",EDGE,"E6.MirrorC"),sQuery(id+"F1.wireOp",EDGE,"E7.MirrorC"),sQuery(id+"F1.wireOp",EDGE,"E8"),sQuery(id+"F1.wireOp",EDGE,"E9.MirrorC"),sQuery(id+"F1.wireOp",EDGE,"E10.MirrorC"),sQuery(id+"F1.wireOp",EDGE,"E11.MirrorC"),sQuery(id+"F1.wireOp",EDGE,"E16"),sQuery(id+"F1.wireOp",EDGE,"E18"),sQuery(id+"F1.wireOp",EDGE,"E20.MirrorCS"),sQuery(id+"F1.wireOp",EDGE,"E22.MirrorCS")])]});
            var Q1;
            Q1=sQuery(id+"F3.wireOp",EDGE,"E26");
            transform(context, id + "F12", {"entities" : qUnion([Q0]), "transformType" : TransformType.ROTATION, "transformAxis" : qUnion([Q1]), "angle" : 45 * degree, "makeCopy" : true});
        }
        {
            var Q0;
            {var subQ0=makeQuery(id+"F2.opExtrude","CAP_FACE",FACE,{"disambiguationData":[OSD([sQuery(id+"F1.wireOp",EDGE,"E1"),sQuery(id+"F1.wireOp",EDGE,"E4.MirrorC"),sQuery(id+"F1.wireOp",EDGE,"E6.MirrorC"),sQuery(id+"F1.wireOp",EDGE,"E7.MirrorC"),sQuery(id+"F1.wireOp",EDGE,"E8"),sQuery(id+"F1.wireOp",EDGE,"E9.MirrorC"),sQuery(id+"F1.wireOp",EDGE,"E10.MirrorC"),sQuery(id+"F1.wireOp",EDGE,"E11.MirrorC"),sQuery(id+"F1.wireOp",EDGE,"E16"),sQuery(id+"F1.wireOp",EDGE,"E18"),sQuery(id+"F1.wireOp",EDGE,"E20.MirrorCS"),sQuery(id+"F1.wireOp",EDGE,"E22.MirrorCS")])],"isStart":false});Q0=makeQuery(id+"F5.opBoolean","MERGE",FACE,{"derivedFrom":[subQ0,makeQuery(id+"F4.opPattern","COPY",FACE,{"derivedFrom":subQ0,"instanceName":"1"})]});}
            var sketch = newSketch(context, id + "F13", { "sketchPlane" : qUnion([Q0])});
            skLineSegment(sketch, "E138.0", {"start": v(-12.62, 7.67) * mm, "end": v(-17.57, 2.72) * mm});
            skLineSegment(sketch, "E138.1", {"start": v(-10.5, 5.55) * mm, "end": v(-15.45, 0.6) * mm});
            skLineSegment(sketch, "E138.2", {"start": v(-15.45, 0.6) * mm, "end": v(-17.57, 2.72) * mm});
            skLineSegment(sketch, "E138.3", {"start": v(-14.83, 3.5) * mm, "end": v(-14.83, 10.5) * mm});
            skLineSegment(sketch, "E138.4", {"start": v(-11.83, 3.5) * mm, "end": v(-11.83, 10.5) * mm});
            skLineSegment(sketch, "E138.5", {"start": v(-14.83, 3.5) * mm, "end": v(-11.83, 3.5) * mm});
            skLineSegment(sketch, "E138.6", {"start": v(-14.83, 10.5) * mm, "end": v(-11.83, 10.5) * mm});
            skLineSegment(sketch, "E138.7", {"start": v(-3.5, 11.35) * mm, "end": v(-10.5, 11.35) * mm});
            skLineSegment(sketch, "E138.8", {"start": v(-10.5, 11.35) * mm, "end": v(-10.5, 14.35) * mm});
            skLineSegment(sketch, "E138.9", {"start": v(-3.5, 14.35) * mm, "end": v(-10.5, 14.35) * mm});
            skLineSegment(sketch, "E138.10", {"start": v(-3.5, 11.35) * mm, "end": v(-3.5, 14.35) * mm});
            skLineSegment(sketch, "E138.11", {"start": v(-5.55, 10.5) * mm, "end": v(-0.6, 15.45) * mm});
            skLineSegment(sketch, "E138.12", {"start": v(-2.72, 17.57) * mm, "end": v(-0.6, 15.45) * mm});
            skLineSegment(sketch, "E138.13", {"start": v(-7.67, 12.62) * mm, "end": v(-2.72, 17.57) * mm});
            skLineSegment(sketch, "E138.14", {"start": v(-7.67, 12.62) * mm, "end": v(-5.55, 10.5) * mm});
            skLineSegment(sketch, "E138.15", {"start": v(-10.5, 5.55) * mm, "end": v(-12.62, 7.67) * mm});
            skLineSegment(sketch, "E139.0", {"start": v(-12.96, -8.01) * mm, "end": v(-17.91, -3.06) * mm});
            skLineSegment(sketch, "E139.1", {"start": v(-17.91, -3.06) * mm, "end": v(-15.79, -0.94) * mm});
            skLineSegment(sketch, "E139.2", {"start": v(-12.96, -8.01) * mm, "end": v(-10.84, -5.9) * mm});
            skLineSegment(sketch, "E139.3", {"start": v(-11.83, -3.5) * mm, "end": v(-11.83, -10.5) * mm});
            skLineSegment(sketch, "E139.4", {"start": v(-11.83, -3.5) * mm, "end": v(-14.83, -3.5) * mm});
            skLineSegment(sketch, "E139.5", {"start": v(-11.83, -10.5) * mm, "end": v(-14.83, -10.5) * mm});
            skLineSegment(sketch, "E139.6", {"start": v(-14.83, -3.5) * mm, "end": v(-14.83, -10.5) * mm});
            skLineSegment(sketch, "E139.7", {"start": v(-10.84, -5.9) * mm, "end": v(-15.79, -0.94) * mm});
            skLineSegment(sketch, "E139.8", {"start": v(5.9, 10.84) * mm, "end": v(0.94, 15.79) * mm});
            skLineSegment(sketch, "E139.9", {"start": v(0.94, 15.79) * mm, "end": v(3.06, 17.91) * mm});
            skLineSegment(sketch, "E139.10", {"start": v(8.01, 12.96) * mm, "end": v(3.06, 17.91) * mm});
            skLineSegment(sketch, "E139.11", {"start": v(5.9, 10.84) * mm, "end": v(8.01, 12.96) * mm});
            skLineSegment(sketch, "E140.0", {"start": v(3.5, 14.35) * mm, "end": v(10.5, 14.35) * mm});
            skLineSegment(sketch, "E140.1", {"start": v(10.5, 14.35) * mm, "end": v(10.5, 11.35) * mm});
            skLineSegment(sketch, "E140.2", {"start": v(3.5, 11.35) * mm, "end": v(10.5, 11.35) * mm});
            skLineSegment(sketch, "E140.3", {"start": v(3.5, 14.35) * mm, "end": v(3.5, 11.35) * mm});
            skLineSegment(sketch, "E141.MirrorCS", {"start": v(12.96, 8.01) * mm, "end": v(17.91, 3.06) * mm});
            skLineSegment(sketch, "E142.MirrorCS", {"start": v(-3.5, -11.83) * mm, "end": v(-10.5, -11.83) * mm});
            skLineSegment(sketch, "E143.MirrorCS", {"start": v(15.79, 0.94) * mm, "end": v(17.91, 3.06) * mm});
            skLineSegment(sketch, "E144.MirrorCS", {"start": v(-8.01, -12.96) * mm, "end": v(-3.06, -17.91) * mm});
            skLineSegment(sketch, "E145.MirrorCS", {"start": v(10.84, 5.9) * mm, "end": v(12.96, 8.01) * mm});
            skLineSegment(sketch, "E146.MirrorCS", {"start": v(14.35, 10.5) * mm, "end": v(11.35, 10.5) * mm});
            skLineSegment(sketch, "E147.MirrorCS", {"start": v(-3.5, -11.83) * mm, "end": v(-3.5, -14.83) * mm});
            skLineSegment(sketch, "E148.MirrorCS", {"start": v(12.62, -7.67) * mm, "end": v(17.57, -2.72) * mm});
            skLineSegment(sketch, "E149.MirrorCS", {"start": v(12.62, -7.67) * mm, "end": v(10.5, -5.55) * mm});
            skLineSegment(sketch, "E150.MirrorCS", {"start": v(-5.9, -10.84) * mm, "end": v(-0.94, -15.79) * mm});
            skLineSegment(sketch, "E151.MirrorCS", {"start": v(5.55, -10.5) * mm, "end": v(7.67, -12.62) * mm});
            skLineSegment(sketch, "E152.MirrorCS", {"start": v(7.67, -12.62) * mm, "end": v(2.72, -17.57) * mm});
            skLineSegment(sketch, "E153.MirrorCS", {"start": v(5.55, -10.5) * mm, "end": v(0.6, -15.45) * mm});
            skLineSegment(sketch, "E154.MirrorCS", {"start": v(0.6, -15.45) * mm, "end": v(2.72, -17.57) * mm});
            skLineSegment(sketch, "E155.MirrorCS", {"start": v(-3.5, -14.83) * mm, "end": v(-10.5, -14.83) * mm});
            skLineSegment(sketch, "E156.MirrorCS", {"start": v(14.35, 3.5) * mm, "end": v(11.35, 3.5) * mm});
            skLineSegment(sketch, "E157.MirrorCS", {"start": v(-8.01, -12.96) * mm, "end": v(-5.9, -10.84) * mm});
            skLineSegment(sketch, "E158.MirrorCS", {"start": v(10.84, 5.9) * mm, "end": v(15.79, 0.94) * mm});
            skLineSegment(sketch, "E159.MirrorCS", {"start": v(-10.5, -11.83) * mm, "end": v(-10.5, -14.83) * mm});
            skLineSegment(sketch, "E160.MirrorCS", {"start": v(11.35, 3.5) * mm, "end": v(11.35, 10.5) * mm});
            skLineSegment(sketch, "E161.MirrorCS", {"start": v(17.57, -2.72) * mm, "end": v(15.45, -0.6) * mm});
            skLineSegment(sketch, "E162.MirrorCS", {"start": v(10.5, -5.55) * mm, "end": v(15.45, -0.6) * mm});
            skLineSegment(sketch, "E163.MirrorCS", {"start": v(11.35, -3.5) * mm, "end": v(14.35, -3.5) * mm});
            skLineSegment(sketch, "E164.MirrorCS", {"start": v(14.35, -3.5) * mm, "end": v(14.35, -10.5) * mm});
            skLineSegment(sketch, "E165.MirrorCS", {"start": v(11.35, -10.5) * mm, "end": v(14.35, -10.5) * mm});
            skLineSegment(sketch, "E166.MirrorCS", {"start": v(11.35, -3.5) * mm, "end": v(11.35, -10.5) * mm});
            skLineSegment(sketch, "E167.MirrorCS", {"start": v(14.35, 3.5) * mm, "end": v(14.35, 10.5) * mm});
            skLineSegment(sketch, "E168.MirrorCS", {"start": v(10.5, -14.83) * mm, "end": v(10.5, -11.83) * mm});
            skLineSegment(sketch, "E169.MirrorCS", {"start": v(3.5, -11.83) * mm, "end": v(10.5, -11.83) * mm});
            skLineSegment(sketch, "E170.MirrorCS", {"start": v(3.5, -14.83) * mm, "end": v(3.5, -11.83) * mm});
            skLineSegment(sketch, "E171.MirrorCS", {"start": v(3.5, -14.83) * mm, "end": v(10.5, -14.83) * mm});
            skLineSegment(sketch, "E172.MirrorCS", {"start": v(-3.06, -17.91) * mm, "end": v(-0.94, -15.79) * mm});
            skSolve(sketch);
        }
        {
            var Q0;
            Q0 = qSketchRegion(id + "F13", true);
            extrude(context, id + "F14", {"entities" : qUnion([Q0]), "operationType" : NewBodyOperationType.REMOVE, "endBound" : BoundingType.THROUGH_ALL, "oppositeDirection" : true, "depth" : 25 * mm});
        }
    });
